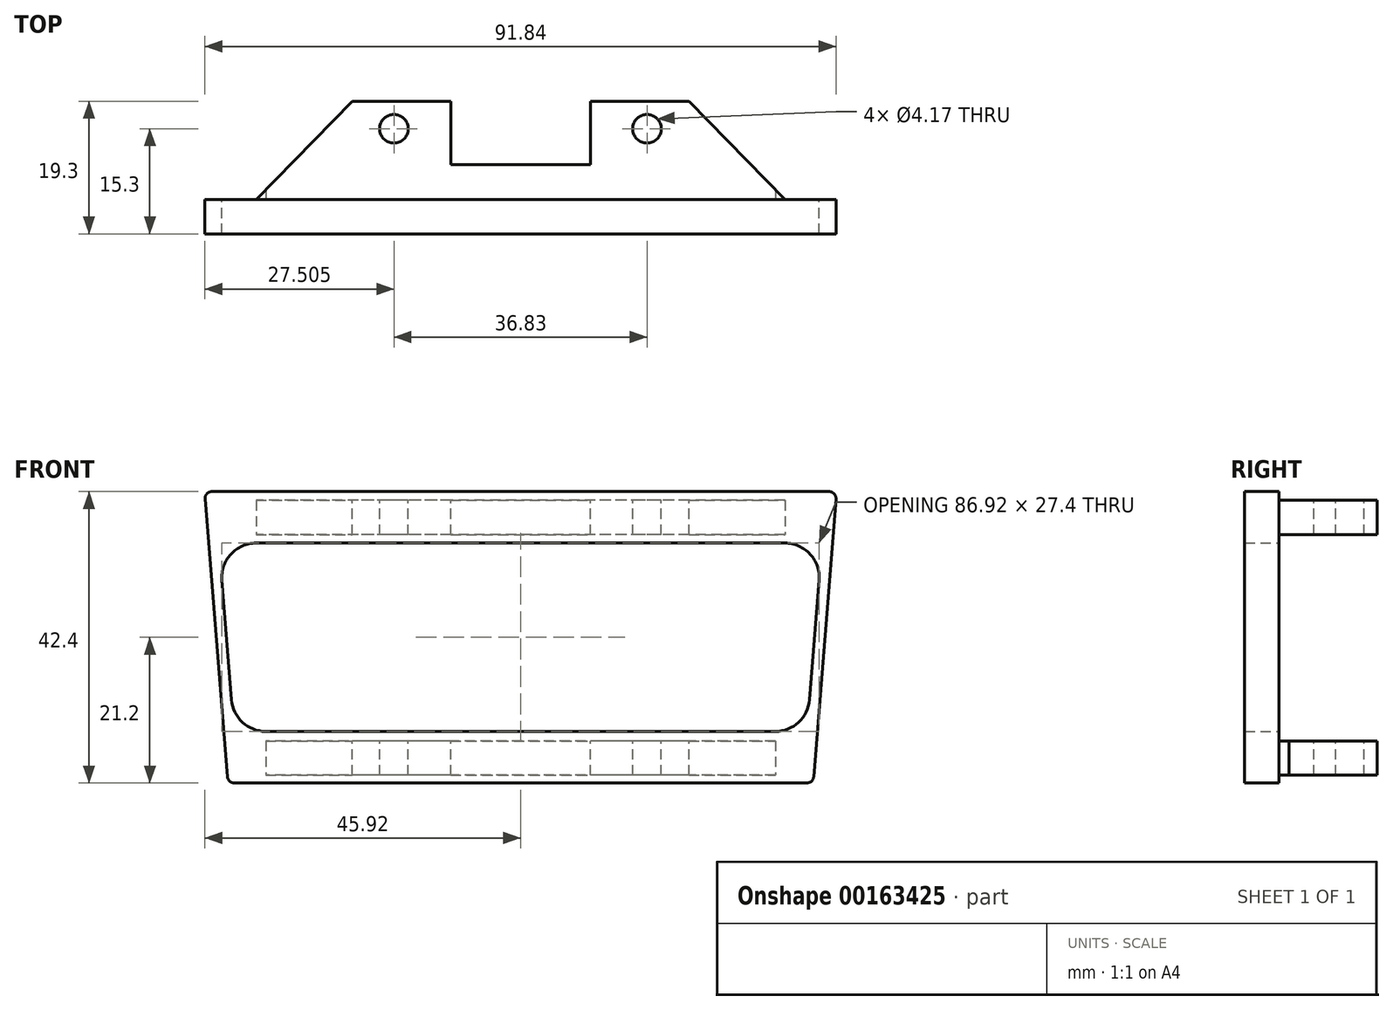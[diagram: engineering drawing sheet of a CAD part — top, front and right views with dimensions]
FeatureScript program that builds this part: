
annotation { "Feature Type Name" : "Feature", "Feature Type Description" : "" }
export const myFeature = defineFeature(function(context is Context, id is Id, definition is map)
    precondition{}
    {
        {
            var Q0;
            Q0=qCreatedBy(makeId("Front.planeOp"),FACE);
            var sketch = newSketch(context, id + "F0", { "sketchPlane" : qUnion([Q0])});
            skLineSegment(sketch, "E0", {"start": v(-0.07, 0.92) * mm, "end": v(-3.31, 41.32) * mm});
            skLineSegment(sketch, "E1", {"start": v(-2.32, 42.4) * mm, "end": v(87.52, 42.4) * mm});
            skLineSegment(sketch, "E2", {"start": v(88.51, 41.32) * mm, "end": v(85.27, 0.92) * mm});
            skLineSegment(sketch, "E3", {"start": v(84.28, 0) * mm, "end": v(0.92, 0) * mm});
            skPoint(sketch, "E4.visualSharp", {"position": v(-3.4, 42.4) * mm});
            skArc(sketch, "E4.filletArc", {"start": v(-2.32, 42.4) * mm, "mid": v(-3.05, 42.08) * mm, "end": v(-3.31, 41.32) * mm});
            skPoint(sketch, "E5.visualSharp", {"position": v(0, 0) * mm});
            skArc(sketch, "E5.filletArc", {"start": v(-0.07, 0.92) * mm, "mid": v(0.24, 0.27) * mm, "end": v(0.92, 0) * mm});
            skPoint(sketch, "E6.visualSharp", {"position": v(85.2, 0) * mm});
            skArc(sketch, "E6.filletArc", {"start": v(84.28, 0) * mm, "mid": v(84.96, 0.27) * mm, "end": v(85.27, 0.92) * mm});
            skPoint(sketch, "E7.visualSharp", {"position": v(88.6, 42.4) * mm});
            skArc(sketch, "E7.filletArc", {"start": v(88.51, 41.32) * mm, "mid": v(88.25, 42.08) * mm, "end": v(87.52, 42.4) * mm});
            skLineSegment(sketch, "E8", {"start": v(4.12, 34.9) * mm, "end": v(81.08, 34.9) * mm});
            skLineSegment(sketch, "E9", {"start": v(86.06, 29.5) * mm, "end": v(84.67, 12.1) * mm});
            skLineSegment(sketch, "E10", {"start": v(79.68, 7.5) * mm, "end": v(5.52, 7.5) * mm});
            skLineSegment(sketch, "E11", {"start": v(0.53, 12.1) * mm, "end": v(-0.86, 29.5) * mm});
            skPoint(sketch, "E12.visualSharp", {"position": v(-1.3, 34.9) * mm});
            skArc(sketch, "E12.filletArc", {"start": v(4.12, 34.9) * mm, "mid": v(0.45, 33.3) * mm, "end": v(-0.86, 29.5) * mm});
            skPoint(sketch, "E13.visualSharp", {"position": v(0.9, 7.5) * mm});
            skArc(sketch, "E13.filletArc", {"start": v(0.53, 12.1) * mm, "mid": v(2.13, 8.83) * mm, "end": v(5.52, 7.5) * mm});
            skPoint(sketch, "E14.visualSharp", {"position": v(84.3, 7.5) * mm});
            skArc(sketch, "E14.filletArc", {"start": v(79.68, 7.5) * mm, "mid": v(83.07, 8.83) * mm, "end": v(84.67, 12.1) * mm});
            skPoint(sketch, "E15.visualSharp", {"position": v(86.5, 34.9) * mm});
            skArc(sketch, "E15.filletArc", {"start": v(86.06, 29.5) * mm, "mid": v(84.75, 33.3) * mm, "end": v(81.08, 34.9) * mm});
            skSolve(sketch);
        }
        {
            var Q0;
            Q0=makeQuery(id+"F0.imprint","IMPRINT",FACE,{"disambiguationData":[TD([[makeQuery(id+"F0.imprint","IMPRINT",EDGE,{"derivedFrom":sQuery(id+"F0.wireOp",EDGE,"E0")}),-1.0]])]});
            extrude(context, id + "F1", {"entities" : qUnion([Q0]), "depth" : 5 * mm});
        }
        {
            var Q0;
            Q0=makeQuery(id+"F1.opExtrude","CAP_FACE",FACE,{"disambiguationData":[OSD([sQuery(id+"F0.wireOp",EDGE,"E0"),sQuery(id+"F0.wireOp",EDGE,"E1"),sQuery(id+"F0.wireOp",EDGE,"E2"),sQuery(id+"F0.wireOp",EDGE,"E3"),sQuery(id+"F0.wireOp",EDGE,"E4.filletArc"),sQuery(id+"F0.wireOp",EDGE,"E5.filletArc"),sQuery(id+"F0.wireOp",EDGE,"E6.filletArc"),sQuery(id+"F0.wireOp",EDGE,"E7.filletArc"),sQuery(id+"F0.wireOp",EDGE,"E8"),sQuery(id+"F0.wireOp",EDGE,"E9"),sQuery(id+"F0.wireOp",EDGE,"E10"),sQuery(id+"F0.wireOp",EDGE,"E11"),sQuery(id+"F0.wireOp",EDGE,"E12.filletArc"),sQuery(id+"F0.wireOp",EDGE,"E13.filletArc"),sQuery(id+"F0.wireOp",EDGE,"E14.filletArc"),sQuery(id+"F0.wireOp",EDGE,"E15.filletArc")])],"isStart":true});
            var sketch = newSketch(context, id + "F2", { "sketchPlane" : qUnion([Q0])});
            skLineSegment(sketch, "E16", {"start": v(-42.6, 42.4) * mm, "end": v(-42.6, 0) * mm, "construction": true});
            skLineSegment(sketch, "E17", {"start": v(-85.36, 21.12) * mm, "end": v(0.19, 21.12) * mm, "construction": true});
            skPoint(sketch, "E17.startSnap0", {"position": v(-86.9, 21.12) * mm});
            skPoint(sketch, "E17.startSnap1", {"position": v(-85.36, 20.8) * mm});
            skPoint(sketch, "E17.endSnap0", {"position": v(1.7, 21.12) * mm});
            skLineSegment(sketch, "E18.bottom", {"start": v(-81.08, 41.12) * mm, "end": v(-4.12, 41.12) * mm});
            skLineSegment(sketch, "E18.top", {"start": v(-81.08, 36.12) * mm, "end": v(-4.12, 36.12) * mm});
            skLineSegment(sketch, "E18.left", {"start": v(-81.08, 41.12) * mm, "end": v(-81.08, 36.12) * mm});
            skLineSegment(sketch, "E18.right", {"start": v(-4.12, 41.12) * mm, "end": v(-4.12, 36.12) * mm});
            skLineSegment(sketch, "E19.bottom", {"start": v(-79.68, 6.12) * mm, "end": v(-5.52, 6.12) * mm});
            skLineSegment(sketch, "E19.top", {"start": v(-79.68, 1.12) * mm, "end": v(-5.52, 1.12) * mm});
            skLineSegment(sketch, "E19.left", {"start": v(-79.68, 6.12) * mm, "end": v(-79.68, 1.12) * mm});
            skLineSegment(sketch, "E19.right", {"start": v(-5.52, 6.12) * mm, "end": v(-5.52, 1.12) * mm});
            skSolve(sketch);
        }
        {
            var Q0;
            Q0=makeQuery(id+"F2.imprint","IMPRINT",FACE,{"disambiguationData":[TD([[makeQuery(id+"F2.imprint","IMPRINT",EDGE,{"derivedFrom":sQuery(id+"F2.wireOp",EDGE,"E18.bottom")}),-1.0]])]});
            var Q1;
            Q1=makeQuery(id+"F2.imprint","IMPRINT",FACE,{"disambiguationData":[TD([[makeQuery(id+"F2.imprint","IMPRINT",EDGE,{"derivedFrom":sQuery(id+"F2.wireOp",EDGE,"E19.bottom")}),-1.0]])]});
            extrude(context, id + "F3", {"entities" : qUnion([Q0, Q1]), "operationType" : NewBodyOperationType.ADD, "depth" : 14.3 * mm});
        }
        {
            var Q0;
            Q0=makeQuery(id+"F3.opExtrude","SWEPT_FACE",FACE,{"disambiguationData":[OSD([sQuery(id+"F2.wireOp",EDGE,"E18.bottom")])]});
            var sketch = newSketch(context, id + "F4", { "sketchPlane" : qUnion([Q0])});
            skLineSegment(sketch, "E20", {"start": v(4.12, 10.3) * mm, "end": v(81.08, 10.3) * mm, "construction": true});
            skCircle(sketch, "E21", {"center": v(24.18, 10.3) * mm, "radius": 2.08 * mm});
            skCircle(sketch, "E22", {"center": v(61.02, 10.3) * mm, "radius": 2.08 * mm});
            skLineSegment(sketch, "E23", {"start": v(42.6, 14.3) * mm, "end": v(42.6, 0) * mm, "construction": true});
            skSolve(sketch);
        }
        {
            var Q0;
            Q0 = qSketchRegion(id + "F4", true);
            extrude(context, id + "F5", {"entities" : qUnion([Q0]), "operationType" : NewBodyOperationType.REMOVE, "endBound" : BoundingType.THROUGH_ALL, "oppositeDirection" : true, "depth" : 25.4 * mm});
        }
        {
            var Q0;
            Q0=makeQuery(id+"F3.opExtrude","SWEPT_FACE",FACE,{"disambiguationData":[OSD([sQuery(id+"F2.wireOp",EDGE,"E18.bottom")])]});
            var sketch = newSketch(context, id + "F6", { "sketchPlane" : qUnion([Q0])});
            skLineSegment(sketch, "E24", {"start": v(4.12, 0) * mm, "end": v(18.1, 14.3) * mm});
            skLineSegment(sketch, "E25", {"start": v(18.1, 14.3) * mm, "end": v(4.12, 14.3) * mm});
            skLineSegment(sketch, "E26", {"start": v(4.12, 14.3) * mm, "end": v(4.12, 0) * mm});
            skLineSegment(sketch, "E27", {"start": v(32.44, 14.3) * mm, "end": v(32.44, 0) * mm});
            skLineSegment(sketch, "E28", {"start": v(52.76, 0) * mm, "end": v(52.76, 14.3) * mm});
            skLineSegment(sketch, "E29", {"start": v(67.1, 14.3) * mm, "end": v(81.08, 0) * mm});
            skLineSegment(sketch, "E30", {"start": v(81.08, 0) * mm, "end": v(81.08, 14.3) * mm});
            skLineSegment(sketch, "E31", {"start": v(81.08, 14.3) * mm, "end": v(67.1, 14.3) * mm});
            skLineSegment(sketch, "E32", {"start": v(32.44, 14.3) * mm, "end": v(52.76, 14.3) * mm});
            skLineSegment(sketch, "E33", {"start": v(32.44, 5.08) * mm, "end": v(52.76, 5.08) * mm});
            skSolve(sketch);
        }
        {
            var Q0;
            Q0 = qSketchRegion(id + "F6", true);
            extrude(context, id + "F7", {"entities" : qUnion([Q0]), "operationType" : NewBodyOperationType.REMOVE, "endBound" : BoundingType.THROUGH_ALL, "oppositeDirection" : true, "depth" : 25.4 * mm});
        }
    });
